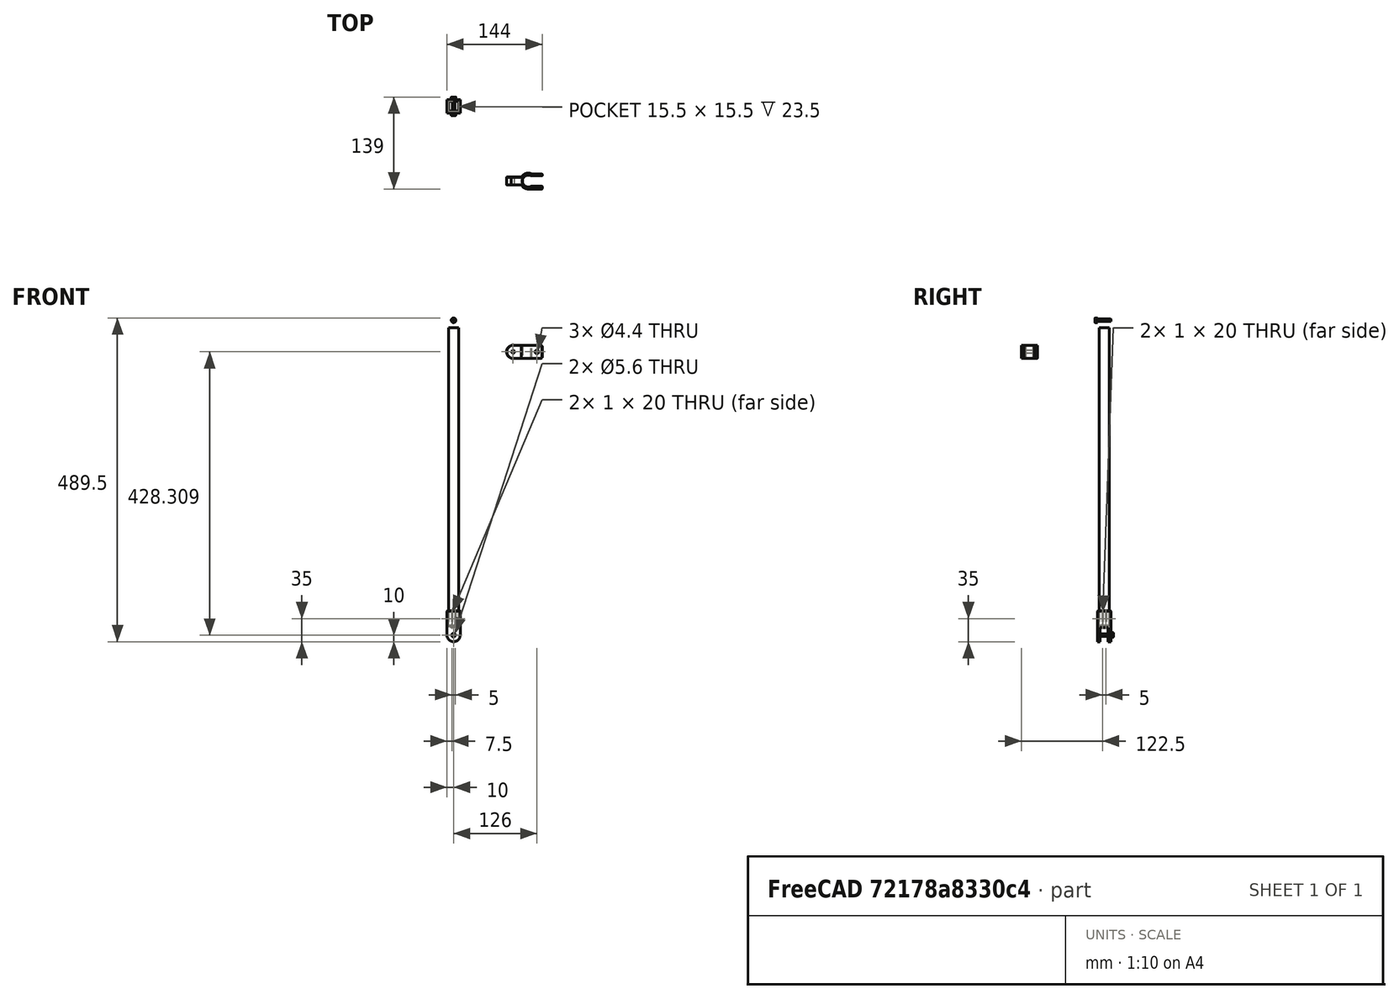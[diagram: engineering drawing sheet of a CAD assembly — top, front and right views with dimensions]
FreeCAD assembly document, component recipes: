
FREECAD ASSEMBLY — COMPONENT RECIPES ("BracePole")

This assembly document has 3 components, labeled P0..P2 below (a component is one placed body or linked part). 3 of them carry a construction recipe — the FreeCAD feature program that regenerates the part from scratch, quoted from this document or its linked companion documents; the rest are supplied as boundary geometry only. No exploded tour is included for this assembly.
COMPONENT P0 — recipe-attached ("SideArm_Pole", modeled in this document).
Construction recipe (the document's own serialized feature program — sketch geometry with constraints, then the solid features built on it; lengths are millimeters unless a unit is written):

FEATURE [PartDesign::AdditiveBox] Box003  label="SideArm_Pole_Base"
  AttacherType = Attacher::AttachEngine3D
  AttachmentOffset = pos=(-7.5,-7.5,0) rot=(0,0,1;0rad)
  Height = 450
  Length = 15
  MapMode = 5
  Placement = pos=(-7.5,-7.5,0) rot=(0,0,1;0rad)
  Support = -> [XY_Plane093]
  Width = 15
  expr: .AttachmentOffset.Base.x = -<<Common>>#<<Parameters>>.pri_bracepole / 2
  expr: .AttachmentOffset.Base.y = -<<Common>>#<<Parameters>>.pri_bracepole / 2
  expr: Height = <<Common>>#<<Parameters>>.pri_bracelength
  expr: Length = <<Common>>#<<Parameters>>.pri_bracepole
  expr: Width = <<Common>>#<<Parameters>>.pri_bracepole
FEATURE [PartDesign::CoordinateSystem] Local_CS310  label="LCSp_SideArm_Pole_Bottom"
  AttacherType = Attacher::AttachEngine3D
  MapMode = 2
  Support = -> [XY_Plane093]
FEATURE [PartDesign::CoordinateSystem] Local_CS311  label="LCSp_SideArm_Pole_Top"
  AttacherType = Attacher::AttachEngine3D
  AttachmentOffset = pos=(0,0,-450) rot=(0,0,1;0rad)
  MapMode = 5
  Placement = pos=(0,0,450) rot=(0,1,0;3.14159rad)
  Support = -> [XY_Plane093]
  expr: .AttachmentOffset.Base.z = -<<Common>>#<<Parameters>>.pri_bracelength
FEATURE [PartDesign::Body] Body022041  label="SideArm_Pole"
  Group = -> [Box003,Local_CS310,Local_CS311]
  Origin = -> Origin094
  Placement = pos=(0,0,15) rot=(0,0,1;0rad)
  Tip = -> Box003
COMPONENT P1 — recipe-attached ("SideArm_PoleClamp", modeled in this document).
Construction recipe (the document's own serialized feature program — sketch geometry with constraints, then the solid features built on it; lengths are millimeters unless a unit is written):

FEATURE [Sketcher::SketchObject] Sketch194  label="SideArm_PoleClamp_Base_Sketch"
  FullyConstrained = true
  MapMode = 5
  Support = -> [XY_Plane094]
  expr: .Constraints.innerdia = <<Common>>#<<Parameters>>.sec_poledia
  expr: Constraints[23] = <<Common>>#<<Parameters>>.sec_poledia - 2
  expr: Constraints[27] = <<Common>>#<<Parameters>>.sec_sidebolt * 2
  expr: Constraints[31] = <<Common>>#<<Parameters>>.sec_fthick
  expr: Constraints[32] = <<Common>>#<<Parameters>>.pri_bracepivotdia - (<<Common>>#<<Parameters>>.sec_fthick + 1) * 2
  expr: Constraints[36] = <<Common>>#<<Parameters>>.sec_poledia
  expr: Constraints[39] = <<Common>>#<<Parameters>>.sec_sidebolt
  expr: Constraints[42] = <<Common>>#<<Parameters>>.sec_fthick + 1
  expr: Constraints[43] = <<Common>>#<<Parameters>>.pri_bracepivotdia + <<Common>>#<<Parameters>>.sec_fthick + <<Common>>#<<Parameters>>.pri_poledia / 2
  sketch-geometry (17):
    g0: ArcOfCircle CenterX=0 CenterY=0 CenterZ=0 NormalX=0 NormalY=0 NormalZ=1 AngleXU=0 Radius=9 StartAngle=1.09491 EndAngle=5.18827
    g1: LineSegment StartX=4.12311 StartY=8 StartZ=0 EndX=21 EndY=8 EndZ=0
    g2: LineSegment StartX=4.12311 StartY=-8 StartZ=0 EndX=21 EndY=-8 EndZ=0
    g3: LineSegment StartX=21 StartY=8 StartZ=0 EndX=21 EndY=10.6667 EndZ=0
    g4: LineSegment StartX=21 StartY=10.6667 StartZ=0 EndX=5.49747 EndY=10.6667 EndZ=0
    g5: ArcOfCircle CenterX=0 CenterY=0 CenterZ=0 NormalX=0 NormalY=0 NormalZ=1 AngleXU=0 Radius=12 StartAngle=1.09491 EndAngle=2.61799
    g6: LineSegment StartX=-10.3923 StartY=6 StartZ=0 EndX=-33 EndY=6 EndZ=0
    g7: LineSegment StartX=-33 StartY=-6 StartZ=0 EndX=-10.3923 EndY=-6 EndZ=0
    g8: LineSegment StartX=21 StartY=-8 StartZ=0 EndX=21 EndY=-12 EndZ=0
    g9: ArcOfCircle CenterX=0 CenterY=0 CenterZ=0 NormalX=0 NormalY=0 NormalZ=1 AngleXU=0 Radius=12 StartAngle=3.66519 EndAngle=4.71239
    g10: LineSegment StartX=-3.33968e-05 StartY=-12 StartZ=0 EndX=21 EndY=-12 EndZ=0
    g11: GeomPoint X=13 Y=10.6667 Z=0
    g12: LineSegment StartX=0 StartY=0 StartZ=0 EndX=5.49747 EndY=10.6667 EndZ=0
    g13: GeomPoint X=-9 Y=0 Z=0
    g14: Circle CenterX=0 CenterY=0 CenterZ=0 NormalX=0 NormalY=0 NormalZ=1 AngleXU=0 Radius=9
    g15: GeomPoint X=9 Y=0 Z=0
    g16: LineSegment StartX=-33 StartY=6 StartZ=0 EndX=-33 EndY=-6 EndZ=0
  constraints (44):
    c: Coincident(g0,g-1)
    c: Diameter(g0) = 18  'innerdia'
    c: Coincident(g1,g0)
    c: Horizontal(g1)
    c: Coincident(g2,g0)
    c: Horizontal(g2)
    c: Coincident(g3,g1)
    c: Vertical(g3)
    c: Horizontal(g4)
    c: Coincident(g5,g0)
    c: Coincident(g5,g4)
    c: Coincident(g6,g5)
    c: Horizontal(g6)
    c: Horizontal(g7)
    c: Coincident(g8,g2)
    c: Vertical(g8)
    c: Coincident(g9,g0)
    c: Coincident(g9,g7)
    c: Coincident(g10,g9)
    c: Horizontal(g10)
    c: Equal(g9,g5)
    c: Symmetric(g6,g7,g-1)
    c: Symmetric(g1,g2,g-1)
    c: DistanceY(g2,g1) = 16
    c: Coincident(g3,g4)
    c: Coincident(g8,g10)
    c: PointOnObject(g11,g4)
    c: DistanceX(g11,g3) = 8
    c: Coincident(g12,g0)
    c: Coincident(g12,g4)
    c: PointOnObject(g0,g12)
    c: Distance(g0,g4) = 3
    c: DistanceY(g7,g6) = 12
    c: PointOnObject(g13,g0)
    c: PointOnObject(g13,g-1)
    c: Coincident(g14,g0)
    c: Diameter(g14) = 18
    c: PointOnObject(g15,g14)
    c: PointOnObject(g15,g-1)
    c: DistanceX(g15,g11) = 4
    c: Coincident(g16,g6)
    c: Coincident(g16,g7)
    c: DistanceY(g8,g8) = 4
    c: DistanceX(g6,g0) = 33
FEATURE [PartDesign::Pad] Pad048  label="SideArm_PoleClamp_Base"
  Direction = (0,0,1)
  Length = 20
  Length2 = 10
  Midplane = true
  Profile = -> Sketch194
  Type = 0
  expr: Length = <<Common>>#<<Parameters>>.pri_bracepivotdia
FEATURE [Sketcher::SketchObject] Sketch195  label="SideArm_PoleClamp_Pivot_Sketch"
  ExternalGeometry = -> [Pad048]
  FullyConstrained = true
  MapMode = 5
  Placement = pos=(0,0,0) rot=(1,0,0;1.5708rad)
  Support = -> [XZ_Plane095]
  expr: Constraints[11] = <<Common>>#<<Parameters>>.pri_bracepivotdia
  expr: Constraints[14] = <<Common>>#<<Parameters>>.sec_sidebolt * 1.1
  expr: Constraints[45] = <<Common>>#<<Parameters>>.pri_fillet
  expr: Constraints[67] = <<Common>>#<<Parameters>>.pri_fillet
  sketch-geometry (28):
    g0: ArcOfCircle CenterX=-23 CenterY=0 CenterZ=0 NormalX=0 NormalY=0 NormalZ=1 AngleXU=0 Radius=10 StartAngle=2.0944 EndAngle=4.18879
    g1: LineSegment StartX=-33 StartY=10 StartZ=0 EndX=21 EndY=10 EndZ=0
    g2: LineSegment StartX=-33 StartY=-10 StartZ=0 EndX=21 EndY=-10 EndZ=0
    g3: LineSegment StartX=-25.6795 StartY=-10 StartZ=0 EndX=-25.6795 EndY=-11 EndZ=0
    g4: LineSegment StartX=-25.6795 StartY=-11 StartZ=0 EndX=-34 EndY=-11 EndZ=0
    g5: LineSegment StartX=-34 StartY=-11 StartZ=0 EndX=-34 EndY=11 EndZ=0
    g6: LineSegment StartX=-34 StartY=11 StartZ=0 EndX=-25.6795 EndY=11 EndZ=0
    g7: LineSegment StartX=-25.6795 StartY=11 StartZ=0 EndX=-25.6795 EndY=10 EndZ=0
    g8: GeomPoint X=-33 Y=0 Z=0
    g9: Circle CenterX=13 CenterY=0 CenterZ=0 NormalX=0 NormalY=0 NormalZ=1 AngleXU=0 Radius=2.2
    g10: ArcOfCircle CenterX=18.5 CenterY=7.5 CenterZ=0 NormalX=0 NormalY=0 NormalZ=1 AngleXU=0 Radius=2.5 StartAngle=0 EndAngle=0.785398
    g11: ArcOfCircle CenterX=18.5 CenterY=-7.5 CenterZ=0 NormalX=0 NormalY=0 NormalZ=1 AngleXU=0 Radius=2.5 StartAngle=5.49779 EndAngle=6.28319
    g12: LineSegment StartX=18.5 StartY=10 StartZ=0 EndX=18.5 EndY=-10 EndZ=0
    g13: LineSegment StartX=18.5 StartY=-7.5 StartZ=0 EndX=21 EndY=-7.5 EndZ=0
    g14: LineSegment StartX=18.5 StartY=7.5 StartZ=0 EndX=21 EndY=7.5 EndZ=0
    g15: LineSegment StartX=19.5355 StartY=10 StartZ=0 EndX=19.5355 EndY=11 EndZ=0
    g16: LineSegment StartX=19.5355 StartY=11 StartZ=0 EndX=22 EndY=11 EndZ=0
    g17: LineSegment StartX=22 StartY=11 StartZ=0 EndX=22 EndY=-11 EndZ=0
    g18: LineSegment StartX=22 StartY=-11 StartZ=0 EndX=19.5355 EndY=-11 EndZ=0
    g19: LineSegment StartX=19.5355 StartY=-11 StartZ=0 EndX=19.5355 EndY=-10 EndZ=0
    g20: LineSegment StartX=21 StartY=-7.5 StartZ=0 EndX=21 EndY=7.5 EndZ=0
    g21: LineSegment StartX=-33 StartY=0 StartZ=0 EndX=-23 EndY=0 EndZ=0
    g22: Circle CenterX=-23 CenterY=0 CenterZ=0 NormalX=0 NormalY=0 NormalZ=1 AngleXU=0 Radius=2.2
    g23: LineSegment StartX=-28 StartY=-8.66025 StartZ=0 EndX=-25.6795 EndY=-10 EndZ=0
    g24: LineSegment StartX=-28 StartY=8.66025 StartZ=0 EndX=-25.6795 EndY=10 EndZ=0
    g25: LineSegment StartX=-25.6795 StartY=10 StartZ=0 EndX=-25.6795 EndY=-10 EndZ=0
    g26: LineSegment StartX=19.5355 StartY=10 StartZ=0 EndX=20.2678 EndY=9.26777 EndZ=0
    g27: LineSegment StartX=19.5355 StartY=-10 StartZ=0 EndX=20.2678 EndY=-9.26777 EndZ=0
  constraints (77):
    c: PointOnObject(g3,g2)
    c: Coincident(g4,g3)
    c: Horizontal(g4)
    c: Coincident(g5,g4)
    c: Vertical(g5)
    c: Coincident(g6,g5)
    c: Horizontal(g6)
    c: Coincident(g7,g6)
    c: Vertical(g7)
    c: Vertical(g3)
    c: Equal(g3,g7)
    c: Diameter(g0) = 20
    c: DistanceY(g7,g7) = 1
    c: DistanceX(g5,g1) = 1
    c: Diameter(g9) = 4.4
    c: Vertical(g12)
    c: Coincident(g13,g11)
    c: Coincident(g13,g11)
    c: Coincident(g14,g10)
    c: Coincident(g14,g10)
    c: Horizontal(g14)
    c: PointOnObject(g10,g12)
    c: PointOnObject(g11,g12)
    c: Horizontal(g13)
    c: Vertical(g15)
    c: Coincident(g16,g15)
    c: Horizontal(g16)
    c: Coincident(g17,g16)
    c: Vertical(g17)
    c: Coincident(g18,g17)
    c: Horizontal(g18)
    c: Vertical(g19)
    c: Coincident(g20,g11)
    c: Coincident(g20,g10)
    c: Equal(g15,g19)
    c: PointOnObject(g6,g16)
    c: DistanceX(g1,g16) = 1
    c: Coincident(g18,g19)
    c: PointOnObject(g8,g0)
    c: Coincident(g21,g8)
    c: Coincident(g21,g0)
    c: Horizontal(g21)
    c: PointOnObject(g3,g7)
    c: PointOnObject(g9,g-1)
    c: DistanceX(g9,g1) = 8
    c: Radius(g10) = 2.5
    c: Coincident(g1,g-3)
    c: Coincident(g2,g-3)
    c: Coincident(g2,g-4)
    c: Coincident(g1,g-4)
    c: PointOnObject(g11,g-3)
    c: PointOnObject(g10,g-3)
    c: PointOnObject(g8,g-4)
    c: Coincident(g22,g0)
    c: Equal(g22,g9)
    c: DistanceX(g0,g-1) = 23  'Clamp_Pivot_Distance'
    c: PointOnObject(g0,g-1)
    c: Tangent(g24,g0) = 1.5708
    c: Tangent(g23,g0) = -1.5708
    c: Tangent(g27,g11) = -1.5708
    c: Tangent(g26,g10) = 1.5708
    c: PointOnObject(g12,g2)
    c: Coincident(g19,g27)
    c: PointOnObject(g12,g1)
    c: Coincident(g15,g26)
    c: Angle(g1,g26) = 2.35619
    c: PointOnObject(g15,g1)
    c: DistanceY(g10,g12) = 2.5
    c: PointOnObject(g19,g2)
    c: Equal(g27,g26)
    c: PointOnObject(g18,g15)
    c: Coincident(g7,g24)
    c: Coincident(g7,g25)
    c: PointOnObject(g7,g1)
    c: Coincident(g3,g23)
    c: Angle(g2,g23) = 2.61799
    c: Coincident(g25,g3)
FEATURE [PartDesign::Pocket] Pocket126  label="SideArm_PoleClamp_Pivot"
  BaseFeature = -> Pad048
  Direction = (0,1,2e-16)
  Length = 5
  Length2 = 5
  Midplane = true
  Profile = -> Sketch195
  Type = 1
FEATURE [PartDesign::CoordinateSystem] Local_CS268  label="LCS_SideClamp_Pivot"
  AttacherType = Attacher::AttachEngine3D
  MapMode = 45
  Placement = pos=(-23,0,1e-16) rot=(0.707107,0,0.707107;3.14159rad)
  Support = -> [Pocket126]
FEATURE [PartDesign::CoordinateSystem] Local_CS269  label="LCS_SideClamp_Bolt"
  AttacherType = Attacher::AttachEngine3D
  MapMode = 11
  Placement = pos=(13,10.6667,2.4e-15) rot=(-0.57735,0.57735,0.57735;2.0944rad)
  Support = -> [Pocket126]
FEATURE [PartDesign::Plane] DatumPlane059  label="DatumPlane_SideClamp_Nut"
  Length = 60.7703
  MapMode = 11
  Placement = pos=(13,-12,-2.7e-15) rot=(0.57735,-0.57735,0.57735;2.0944rad)
  ResizeMode = 0
  Support = -> [Pocket126]
  Width = 68.7703
FEATURE [Sketcher::SketchObject] Sketch238  label="SideArm_PoleClamp_BraceNut_Sketch"
  FullyConstrained = true
  MapMode = 5
  Placement = pos=(13,-12,-2.7e-15) rot=(-0.57735,0.57735,-0.57735;4.18879rad)
  Support = -> [DatumPlane059]
  expr: Constraints[1] = <<Common>>#<<Parameters>>.acc_M4Bore
  sketch-geometry (1):
    g0: Circle CenterX=0 CenterY=0 CenterZ=0 NormalX=0 NormalY=0 NormalZ=1 AngleXU=0 Radius=2.8
  constraints (2):
    c: Coincident(g0,g-1)
    c: Diameter(g0) = 5.6
FEATURE [PartDesign::Pocket] Pocket188  label="SideArm_PoleClamp_BraceNut"
  BaseFeature = -> Pocket126
  Direction = (0,1,0)
  Length = 4
  Length2 = 100
  Profile = -> Sketch238
  Type = 0
FEATURE [PartDesign::CoordinateSystem] Local_CS320  label="LCS_SideClamp_Nut"
  AttacherType = Attacher::AttachEngine3D
  MapMode = 11
  Placement = pos=(13,-12,-2.7e-15) rot=(-0.57735,0.57735,0.57735;2.0944rad)
  Support = -> [Pocket126]
FEATURE [PartDesign::Chamfer] Chamfer001  label="SideArm_Chamfer"
  Angle = 45
  Base = -> Pocket188 [Edge6,Edge37,Edge36,Edge35,Edge32,Edge33,Edge31,Edge29,Edge28,Edge10,Edge12,Edge9,Edge13,Edge14,Edge16,Edge17,Edge18,Edge1,Edge5,Edge4,Edge3,Edge2,Edge26,Edge24,Edge22,Edge20,Edge66,Edge68,Edge67,Edge65,Edge62,Edge58,Edge60,Edge59,Edge57,Edge56,Edge47,Edge42,Edge41,Edge49,+6 more]
  BaseFeature = -> Pocket188
  ChamferType = 0
  FlipDirection = false
  Size = 0.4
  Size2 = 1
  SupportTransform = false
  UseAllEdges = false
FEATURE [PartDesign::Body] Body022042  label="SideArm_PoleClamp"
  Group = -> [Sketch194,Pad048,Sketch195,Pocket126,Local_CS268,Local_CS269,Sketch238,DatumPlane059,Pocket188,Local_CS320,Chamfer001]
  Origin = -> Origin095
  Placement = pos=(113,-113,428.309) rot=(0,0,1;0rad)
  Tip = -> Chamfer001
  expr: .Placement.Base.x = <<Common>>#<<Parameters>>.bolt_x
  expr: .Placement.Base.y = -<<Common>>#<<Parameters>>.bolt_y
  expr: .Placement.Base.z = <<Common>>#<<Parameters>>.pri_braceclamp_z
COMPONENT P2 — recipe-attached ("SideArm_Pivot_Outer_Square", modeled in this document).
Construction recipe (the document's own serialized feature program — sketch geometry with constraints, then the solid features built on it; lengths are millimeters unless a unit is written):

FEATURE [Sketcher::SketchObject] Sketch263  label="SideArm_Outer_YZ_Sketch"
  FullyConstrained = true
  MapMode = 5
  Placement = pos=(0,0,0) rot=(0.57735,0.57735,0.57735;2.0944rad)
  Support = -> [YZ_Plane113]
  expr: Constraints[12] = -<<Common>>#<<Parameters>>.pri_bracepivotdia / 2 - 1
  expr: Constraints[19] = <<Common>>#<<Parameters>>.pri_bracepivotdia / 2 + <<Common>>#<<Parameters>>.sec_fthick / 2
  expr: Constraints[22] = max(<<Common>>#<<Parameters>>.pri_bracepole + <<Common>>#<<Parameters>>.sec_fthick; <<Common>>#<<Parameters>>.pri_bracepivotdia + 1) + 2
  expr: Constraints[23] = <<Common>>#<<Parameters>>.pri_bracepivotdia
  expr: Constraints[35] = <<Common>>#<<Parameters>>.sec_fthick + 1
  sketch-geometry (14):
    g0: LineSegment StartX=-6 StartY=11.5 StartZ=0 EndX=-6 EndY=-11 EndZ=0
    g1: LineSegment StartX=-6 StartY=-11 StartZ=0 EndX=6 EndY=-11 EndZ=0
    g2: LineSegment StartX=6 StartY=-11 StartZ=0 EndX=6 EndY=11.5 EndZ=0
    g3: LineSegment StartX=10 StartY=11.5 StartZ=0 EndX=11.5 EndY=13 EndZ=0
    g4: LineSegment StartX=11.5 StartY=13 StartZ=0 EndX=11.5 EndY=-13 EndZ=0
    g5: LineSegment StartX=11.5 StartY=-13 StartZ=0 EndX=-11.5 EndY=-13 EndZ=0
    g6: LineSegment StartX=-11.5 StartY=-13 StartZ=0 EndX=-11.5 EndY=13 EndZ=0
    g7: LineSegment StartX=-11.5 StartY=13 StartZ=0 EndX=-10 EndY=11.5 EndZ=0
    g8: LineSegment StartX=-6 StartY=11.5 StartZ=0 EndX=6 EndY=11.5 EndZ=0
    g9: LineSegment StartX=-11.5 StartY=13 StartZ=0 EndX=11.5 EndY=13 EndZ=0
    g10: LineSegment StartX=-10 StartY=11.5 StartZ=0 EndX=-10 EndY=-11 EndZ=0
    g11: LineSegment StartX=10 StartY=11.5 StartZ=0 EndX=10 EndY=-11 EndZ=0
    g12: LineSegment StartX=10 StartY=-11 StartZ=0 EndX=6 EndY=-11 EndZ=0
    g13: LineSegment StartX=-10 StartY=-11 StartZ=0 EndX=-6 EndY=-11 EndZ=0
  constraints (39):
    c: Vertical(g0)
    c: Coincident(g1,g0)
    c: Horizontal(g1)
    c: Coincident(g2,g1)
    c: Vertical(g2)
    c: Coincident(g4,g3)
    c: Vertical(g4)
    c: Coincident(g5,g4)
    c: Horizontal(g5)
    c: Coincident(g6,g5)
    c: Vertical(g6)
    c: Coincident(g7,g6)
    c: DistanceY(g1) = -11
    c: Coincident(g8,g0)
    c: Coincident(g8,g2)
    c: Coincident(g9,g6)
    c: Coincident(g9,g3)
    c: Horizontal(g8)
    c: Equal(g7,g3)
    c: DistanceY(g2) = 11.5
    c: Symmetric(g3,g6,g-2)
    c: DistanceY(g4,g1) = 2
    c: DistanceX(g5,g5) = 23
    c: DistanceX(g7,g3) = 20
    c: Vertical(g10)
    c: Coincident(g11,g3)
    c: Vertical(g11)
    c: Coincident(g12,g11)
    c: Coincident(g12,g2)
    c: Horizontal(g12)
    c: Coincident(g13,g10)
    c: Coincident(g13,g0)
    c: Horizontal(g13)
    c: Coincident(g10,g7)
    c: Equal(g12,g13)
    c: DistanceX(g12,g12) = 4
    c: PointOnObject(g7,g8)
    c: PointOnObject(g3,g8)
    c: Angle(g3,g4) = 0.785398
FEATURE [Sketcher::SketchObject] Sketch264  label="SideArm_Outer_Profile_XZ_Sketch"
  FullyConstrained = true
  MapMode = 5
  Placement = pos=(0,0,0) rot=(1,0,0;1.5708rad)
  Support = -> [XZ_Plane113]
  expr: Constraints[10] = <<Common>>#<<Parameters>>.pri_bracepivotdia
  expr: Constraints[13] = <<Common>>#<<Parameters>>.pri_bracepivotdia / 2 + <<Common>>#<<Parameters>>.sec_fthick / 2
  expr: Constraints[15] = <<Common>>#<<Parameters>>.pri_bracepivotdia
  expr: Constraints[18] = min(<<Common>>#<<Parameters>>.pri_bracepole + <<Common>>#<<Parameters>>.sec_fthick * 2; 20)
  expr: Constraints[22] = max(0.5; abs(20 - <<Common>>#<<Parameters>>.pri_bracepivotdia) / 2)
  expr: Constraints[27] = <<Common>>#<<Parameters>>.sec_sidebolt * 1.1
  sketch-geometry (11):
    g0: ArcOfCircle CenterX=0 CenterY=0 CenterZ=0 NormalX=0 NormalY=0 NormalZ=1 AngleXU=0 Radius=10 StartAngle=3.1416 EndAngle=6.28319
    g1: LineSegment StartX=10 StartY=-2.4e-15 StartZ=0 EndX=10 EndY=11.5 EndZ=0
    g2: LineSegment StartX=-10 StartY=-4.17172e-05 StartZ=0 EndX=-10 EndY=11.5 EndZ=0
    g3: LineSegment StartX=-10 StartY=11.5 StartZ=0 EndX=-10 EndY=12 EndZ=0
    g4: LineSegment StartX=-10 StartY=12 StartZ=0 EndX=-10 EndY=36.5 EndZ=0
    g5: LineSegment StartX=-10 StartY=36.5 StartZ=0 EndX=10 EndY=36.5 EndZ=0
    g6: LineSegment StartX=10 StartY=36.5 StartZ=0 EndX=10 EndY=12 EndZ=0
    g7: LineSegment StartX=10 StartY=12 StartZ=0 EndX=10 EndY=11.5 EndZ=0
    g8: LineSegment StartX=0 StartY=0 StartZ=0 EndX=10 EndY=-2.4e-15 EndZ=0
    g9: LineSegment StartX=-10 StartY=12 StartZ=0 EndX=10 EndY=12 EndZ=0
    g10: Circle CenterX=0 CenterY=0 CenterZ=0 NormalX=0 NormalY=0 NormalZ=1 AngleXU=0 Radius=2.2
  constraints (28):
    c: Coincident(g0,g-1)
    c: Coincident(g1,g0)
    c: Coincident(g3,g2)
    c: Coincident(g4,g3)
    c: Vertical(g4)
    c: Coincident(g5,g4)
    c: Coincident(g6,g5)
    c: Coincident(g7,g6)
    c: Coincident(g7,g1)
    c: Vertical(g6)
    c: Diameter(g0) = 20
    c: Coincident(g8,g0)
    c: Coincident(g8,g0)
    c: DistanceY(g-1,g1) = 11.5
    c: Symmetric(g2,g1,g-2)
    c: DistanceX(g2,g1) = 20
    c: Perpendicular(g1,g8)
    c: Symmetric(g4,g5,g-2)
    c: DistanceX(g5,g5) = 20
    c: Coincident(g9,g3)
    c: Coincident(g9,g6)
    c: Horizontal(g9)
    c: DistanceY(g2,g3) = 0.5
    c: DistanceY(g1,g5) = 25
    c: Coincident(g0,g2)
    c: Vertical(g2)
    c: Coincident(g10,g0)
    c: Diameter(g10) = 4.4
FEATURE [Sketcher::SketchObject] Sketch265  label="SideArm_Outer_Shaft_Sketch"
  AttachmentOffset = pos=(0,0,13) rot=(0,0,1;0rad)
  FullyConstrained = true
  MapMode = 5
  Placement = pos=(0,0,13) rot=(0,0,1;0rad)
  Support = -> [XY_Plane113]
  expr: .AttachmentOffset.Base.z = <<Common>>#<<Parameters>>.pri_bracepivotdia / 2 + <<Common>>#<<Parameters>>.sec_fthick * 1 + (20 - <<Common>>#<<Parameters>>.pri_bracepivotdia) / 2
  expr: Constraints[9] = <<Common>>#<<Parameters>>.pri_bracepole + <<Common>>#<<Parameters>>.pri_tol
  sketch-geometry (4):
    g0: LineSegment StartX=-7.75 StartY=7.75 StartZ=0 EndX=7.75 EndY=7.75 EndZ=0
    g1: LineSegment StartX=7.75 StartY=7.75 StartZ=0 EndX=7.75 EndY=-7.75 EndZ=0
    g2: LineSegment StartX=7.75 StartY=-7.75 StartZ=0 EndX=-7.75 EndY=-7.75 EndZ=0
    g3: LineSegment StartX=-7.75 StartY=-7.75 StartZ=0 EndX=-7.75 EndY=7.75 EndZ=0
  constraints (10):
    c: Coincident(g0,g1)
    c: Coincident(g1,g2)
    c: Coincident(g2,g3)
    c: Coincident(g3,g0)
    c: Horizontal(g2)
    c: Vertical(g3)
    c: Equal(g0,g1)
    c: Symmetric(g0,g0,g-2)
    c: Symmetric(g0,g1,g-1)
    c: DistanceX(g0,g0) = 15.5
FEATURE [PartDesign::CoordinateSystem] Local_CS315  label="LCSp_Sidearm_Pivot_Lower001"
  AttacherType = Attacher::AttachEngine3D
  MapMode = 5
  Placement = pos=(0,0,0) rot=(0,1,0;3.14159rad)
  Support = -> [XY_Plane113]
FEATURE [PartDesign::CoordinateSystem] Local_CS316  label="LCSp_Sidearm_Pivot_LowerTilt001"
  AttacherType = Attacher::AttachEngine3D
  AttachmentOffset = pos=(0,0,0) rot=(0,-1,0;0.440587rad)
  MapMode = 5
  Placement = pos=(0,0,0) rot=(0,1,0;2.70101rad)
  Support = -> [Local_CS315]
  expr: .AttachmentOffset.Rotation.Pitch = -<<Common>>#<<Parameters>>.pri_bracetilt
FEATURE [PartDesign::Pad] Pad066  label="SideArm_Outer_Body"
  Direction = (0,-1,-2e-16)
  Length = 20
  Length2 = 100
  Midplane = true
  Placement = pos=(0,0,0) rot=(1,0,0;1.5708rad)
  Profile = -> Sketch264
  Type = 0
  expr: Length = min(<<Common>>#<<Parameters>>.pri_bracepole + <<Common>>#<<Parameters>>.sec_fthick * 2; 20)
FEATURE [PartDesign::Pocket] Pocket176  label="SideArm_Outer_YZ_Cut"
  BaseFeature = -> Pad066
  Direction = (-1,2e-16,-3e-16)
  Length = 5
  Length2 = 100
  Midplane = true
  Placement = pos=(0,0,0) rot=(1,0,0;1.5708rad)
  Profile = -> Sketch263
  Type = 1
FEATURE [PartDesign::Pocket] Pocket177  label="SideArm_Outer_Shaft"
  BaseFeature = -> Pocket176
  Direction = (0,0,-1)
  Length = 5
  Length2 = 100
  Placement = pos=(0,0,0) rot=(1,0,0;1.5708rad)
  Profile = -> Sketch265
  Reversed = true
  Type = 1
FEATURE [PartDesign::AdditiveCylinder] Cylinder014  label="SideArm_Outer_GripCylinderX1"
  Angle = 360
  AttacherType = Attacher::AttachEngine3D
  AttachmentOffset = pos=(7.75,-2.5,15) rot=(0,0,1;0rad)
  BaseFeature = -> Pocket177
  FirstAngle = 0
  Height = 20
  MapMode = 5
  Placement = pos=(7.75,-2.5,15) rot=(0,0,1;0rad)
  Radius = 0.5
  SecondAngle = 0
  Support = -> [XY_Plane113]
  expr: .AttachmentOffset.Base.x = (<<Common>>#<<Parameters>>.pri_bracepole + <<Common>>#<<Parameters>>.pri_tol) / 2
  expr: .AttachmentOffset.Base.z = <<Common>>#<<Parameters>>.pri_bracepivotdia / 2 + <<Common>>#<<Parameters>>.sec_fthick * 1 + (20 - <<Common>>#<<Parameters>>.pri_bracepivotdia) / 2 + 2
FEATURE [PartDesign::AdditiveCylinder] Cylinder015  label="SideArrn_Outer_GripCylinderX2"
  Angle = 360
  AttacherType = Attacher::AttachEngine3D
  AttachmentOffset = pos=(7.75,2.5,15) rot=(0,0,1;0rad)
  BaseFeature = -> Cylinder014
  FirstAngle = 0
  Height = 20
  MapMode = 5
  Placement = pos=(7.75,2.5,15) rot=(0,0,1;0rad)
  Radius = 0.5
  SecondAngle = 0
  Support = -> [XY_Plane113]
  expr: .AttachmentOffset.Base.x = (<<Common>>#<<Parameters>>.pri_bracepole + <<Common>>#<<Parameters>>.pri_tol) / 2
  expr: .AttachmentOffset.Base.z = <<Common>>#<<Parameters>>.pri_bracepivotdia / 2 + <<Common>>#<<Parameters>>.sec_fthick * 1 + (20 - <<Common>>#<<Parameters>>.pri_bracepivotdia) / 2 + 2
FEATURE [PartDesign::PolarPattern] PolarPattern005  label="SideArm_Outer_GripCylinder"
  Angle = 360
  Axis = -> Z_Axis113
  BaseFeature = -> Cylinder015
  Occurrences = 4
  Originals = -> [Cylinder014,Cylinder015]
  Placement = pos=(7.75,2.5,15) rot=(0,0,1;0rad)
FEATURE [PartDesign::CoordinateSystem] Local_CS317  label="LCSp_SideArm_Pivot_OuterTilt"
  AttacherType = Attacher::AttachEngine3D
  AttachmentOffset = pos=(0,0,0) rot=(0,1,0;0.440587rad)
  MapMode = 5
  Placement = pos=(0,0,0) rot=(0,1,0;3.58218rad)
  Support = -> [Local_CS315]
  expr: .AttachmentOffset.Rotation.Pitch = <<Common>>#<<Parameters>>.pri_bracetilt
FEATURE [Sketcher::SketchObject] Sketch268  label="SideArm_Outer_SupportA_Sketch"
  AttachmentOffset = pos=(0,0,14.5) rot=(0,0,1;0rad)
  FullyConstrained = true
  MapMode = 5
  Placement = pos=(0,0,14.5) rot=(0,0,1;0rad)
  Support = -> [XY_Plane113]
  expr: .AttachmentOffset.Base.z = <<Common>>#<<Parameters>>.pri_bracepivotdia / 2 + <<Common>>#<<Parameters>>.sec_fthick * 1.5 + (20 - <<Common>>#<<Parameters>>.pri_bracepivotdia) / 2
  sketch-geometry (4):
    g0: LineSegment StartX=-2.25 StartY=2.25 StartZ=0 EndX=2.25 EndY=2.25 EndZ=0
    g1: LineSegment StartX=2.25 StartY=2.25 StartZ=0 EndX=2.25 EndY=-2.25 EndZ=0
    g2: LineSegment StartX=2.25 StartY=-2.25 StartZ=0 EndX=-2.25 EndY=-2.25 EndZ=0
    g3: LineSegment StartX=-2.25 StartY=-2.25 StartZ=0 EndX=-2.25 EndY=2.25 EndZ=0
  constraints (10):
    c: Coincident(g0,g1)
    c: Coincident(g1,g2)
    c: Coincident(g2,g3)
    c: Coincident(g3,g0)
    c: Horizontal(g0)
    c: Vertical(g3)
    c: Symmetric(g1,g0,g-1)
    c: Symmetric(g1,g2,g-2)
    c: Equal(g0,g3)
    c: DistanceY(g1,g1) = 4.5
FEATURE [Sketcher::SketchObject] Sketch269  label="SideArm_Outer_SupportB_Sketch"
  AttachmentOffset = pos=(0,0,14.75) rot=(0,0,1;0rad)
  FullyConstrained = true
  MapMode = 5
  Placement = pos=(0,0,14.75) rot=(0,0,1;0rad)
  Support = -> [XY_Plane113]
  expr: .AttachmentOffset.Base.z = <<Common>>#<<Parameters>>.pri_bracepivotdia / 2 + <<Common>>#<<Parameters>>.sec_fthick * 1.5 + (20 - <<Common>>#<<Parameters>>.pri_bracepivotdia) / 2 + 0.25
  expr: Constraints[8] = <<Common>>#<<Parameters>>.pri_bracepole + <<Common>>#<<Parameters>>.pri_tol
  sketch-geometry (13):
    g0: LineSegment StartX=-7.75 StartY=7.75 StartZ=0 EndX=7.75 EndY=7.75 EndZ=0
    g1: LineSegment StartX=7.75 StartY=7.75 StartZ=0 EndX=7.75 EndY=-7.75 EndZ=0
    g2: LineSegment StartX=7.75 StartY=-7.75 StartZ=0 EndX=-7.75 EndY=-7.75 EndZ=0
    g3: LineSegment StartX=-7.75 StartY=-7.75 StartZ=0 EndX=-7.75 EndY=7.75 EndZ=0
    g4: LineSegment StartX=-6.75 StartY=2.25 StartZ=0 EndX=2.25 EndY=2.25 EndZ=0
    g5: LineSegment StartX=-2.25 StartY=-2.25 StartZ=0 EndX=6.75 EndY=-2.25 EndZ=0
    g6: LineSegment StartX=-3.25 StartY=7.75 StartZ=0 EndX=7.75 EndY=-3.25 EndZ=0
    g7: LineSegment StartX=-7.75 StartY=3.25 StartZ=0 EndX=3.25 EndY=-7.75 EndZ=0
    g8: GeomPoint X=0 Y=2.25 Z=0
    g9: GeomPoint X=0 Y=-2.25 Z=0
    g10: LineSegment StartX=-2.25 StartY=-2.25 StartZ=0 EndX=2.25 EndY=2.25 EndZ=0
    g11: LineSegment StartX=-6.75 StartY=2.25 StartZ=0 EndX=-2.25 EndY=-2.25 EndZ=0
    g12: LineSegment StartX=2.25 StartY=2.25 StartZ=0 EndX=6.75 EndY=-2.25 EndZ=0
  constraints (35):
    c: Coincident(g0,g1)
    c: Coincident(g1,g2)
    c: Coincident(g2,g3)
    c: Coincident(g3,g0)
    c: Horizontal(g0)
    c: Vertical(g3)
    c: Symmetric(g0,g1,g-1)
    c: Symmetric(g1,g2,g-2)
    c: DistanceX(g2,g2) = 15.5
    c: Equal(g1,g2)
    c: Horizontal(g4)
    c: Horizontal(g5)
    c: PointOnObject(g6,g0)
    c: PointOnObject(g6,g1)
    c: PointOnObject(g7,g3)
    c: PointOnObject(g7,g2)
    c: PointOnObject(g8,g4)
    c: PointOnObject(g9,g5)
    c: PointOnObject(g9,g-2)
    c: Symmetric(g8,g9,g-1)
    c: DistanceY(g9,g8) = 4.5
    c: Coincident(g10,g5)
    c: Coincident(g10,g4)
    c: PointOnObject(g-1,g10)
    c: Angle(g10) = 0.785398
    c: PointOnObject(g5,g7)
    c: Perpendicular(g10,g7)
    c: PointOnObject(g4,g6)
    c: Perpendicular(g10,g6)
    c: PointOnObject(g4,g7)
    c: PointOnObject(g5,g6)
    c: Coincident(g11,g4)
    c: Coincident(g11,g5)
    c: Coincident(g12,g4)
    c: Coincident(g12,g5)
FEATURE [Sketcher::SketchObject] Sketch270  label="SideArm_Outer_SupportC_Sketch"
  AttachmentOffset = pos=(0,0,15) rot=(0,0,1;0rad)
  FullyConstrained = true
  MapMode = 5
  Placement = pos=(0,0,15) rot=(0,0,1;0rad)
  Support = -> [XY_Plane113]
  expr: .AttachmentOffset.Base.z = <<Common>>#<<Parameters>>.pri_bracepivotdia / 2 + <<Common>>#<<Parameters>>.sec_fthick * 1.5 + (20 - <<Common>>#<<Parameters>>.pri_bracepivotdia) / 2 + 0.5
  expr: Constraints[19] = <<Common>>#<<Parameters>>.pri_bracepole + <<Common>>#<<Parameters>>.pri_tol
  sketch-geometry (13):
    g0: LineSegment StartX=-2.25 StartY=2.25 StartZ=0 EndX=2.25 EndY=2.25 EndZ=0
    g1: LineSegment StartX=2.25 StartY=2.25 StartZ=0 EndX=2.25 EndY=-2.25 EndZ=0
    g2: LineSegment StartX=2.25 StartY=-2.25 StartZ=0 EndX=-2.25 EndY=-2.25 EndZ=0
    g3: LineSegment StartX=-2.25 StartY=-2.25 StartZ=0 EndX=-2.25 EndY=2.25 EndZ=0
    g4: LineSegment StartX=-7.75 StartY=7.75 StartZ=0 EndX=7.75 EndY=7.75 EndZ=0
    g5: LineSegment StartX=7.75 StartY=7.75 StartZ=0 EndX=7.75 EndY=-7.75 EndZ=0
    g6: LineSegment StartX=7.75 StartY=-7.75 StartZ=0 EndX=-7.75 EndY=-7.75 EndZ=0
    g7: LineSegment StartX=-7.75 StartY=-7.75 StartZ=0 EndX=-7.75 EndY=7.75 EndZ=0
    g8: LineSegment StartX=-3.25 StartY=7.75 StartZ=0 EndX=7.75 EndY=-3.25 EndZ=0
    g9: LineSegment StartX=-7.75 StartY=3.25 StartZ=0 EndX=3.25 EndY=-7.75 EndZ=0
    g10: LineSegment StartX=-2.25 StartY=-2.25 StartZ=0 EndX=2.25 EndY=2.25 EndZ=0
    g11: LineSegment StartX=-7.75 StartY=3.25 StartZ=0 EndX=-3.25 EndY=7.75 EndZ=0
    g12: LineSegment StartX=3.25 StartY=-7.75 StartZ=0 EndX=7.75 EndY=-3.25 EndZ=0
  constraints (34):
    c: Coincident(g0,g1)
    c: Coincident(g1,g2)
    c: Coincident(g2,g3)
    c: Coincident(g3,g0)
    c: Horizontal(g0)
    c: Vertical(g3)
    c: Symmetric(g2,g1,g-2)
    c: Symmetric(g1,g0,g-1)
    c: Equal(g1,g2)
    c: DistanceY(g1,g1) = 4.5
    c: Coincident(g4,g5)
    c: Coincident(g5,g6)
    c: Coincident(g6,g7)
    c: Coincident(g7,g4)
    c: Horizontal(g4)
    c: Vertical(g7)
    c: Symmetric(g5,g6,g-2)
    c: Symmetric(g4,g5,g-1)
    c: Equal(g5,g6)
    c: DistanceY(g5,g5) = 15.5
    c: PointOnObject(g8,g4)
    c: PointOnObject(g8,g5)
    c: PointOnObject(g9,g7)
    c: PointOnObject(g9,g6)
    c: PointOnObject(g2,g9)
    c: PointOnObject(g0,g8)
    c: Coincident(g10,g2)
    c: Coincident(g10,g0)
    c: Perpendicular(g8,g10)
    c: Perpendicular(g9,g10)
    c: Coincident(g11,g9)
    c: Coincident(g11,g8)
    c: Coincident(g12,g9)
    c: Coincident(g12,g8)
FEATURE [Sketcher::SketchObject] Sketch271  label="SideArm_Outer_Nut_Sketch"
  AttachmentOffset = pos=(0,0,10) rot=(0,0,1;0rad)
  FullyConstrained = true
  MapMode = 5
  Placement = pos=(0,-10,-2.2e-15) rot=(1,0,0;1.5708rad)
  Support = -> [XZ_Plane113]
  expr: Constraints[1] = <<Common>>#<<Parameters>>.acc_M4Bore
  sketch-geometry (1):
    g0: Circle CenterX=0 CenterY=0 CenterZ=0 NormalX=0 NormalY=0 NormalZ=1 AngleXU=0 Radius=2.8
  constraints (2):
    c: Coincident(g0,g-1)
    c: Diameter(g0) = 5.6
FEATURE [Sketcher::SketchObject] Sketch272  label="SideArm_Outer_Counterbore_Sketch"
  AttachmentOffset = pos=(0,0,-10) rot=(0,0,1;0rad)
  FullyConstrained = true
  MapMode = 5
  Placement = pos=(0,10,2.2e-15) rot=(1,0,0;1.5708rad)
  Support = -> [XZ_Plane113]
  sketch-geometry (1):
    g0: Circle CenterX=0 CenterY=0 CenterZ=0 NormalX=0 NormalY=0 NormalZ=1 AngleXU=0 Radius=4.5
  constraints (2):
    c: Coincident(g0,g-1)
    c: Radius(g0) = 4.5
FEATURE [PartDesign::Pocket] Pocket189  label="SideArm_Outer_Nut"
  BaseFeature = -> PolarPattern005
  Direction = (0,1,2e-16)
  Length = 4
  Length2 = 100
  Placement = pos=(7.75,2.5,15) rot=(0,0,1;0rad)
  Profile = -> Sketch271
  Type = 0
FEATURE [PartDesign::CoordinateSystem] Local_CS  label="LCS_SideArm_Outer_Nut"
  AttacherType = Attacher::AttachEngine3D
  MapMode = 11
  Placement = pos=(0,-10,-2e-15) rot=(0.57735,-0.57735,-0.57735;4.18879rad)
  Support = -> [Pocket189]
FEATURE [PartDesign::CoordinateSystem] Local_CS318  label="LCS_SideArm_Outer_Screw"
  AttacherType = Attacher::AttachEngine3D
  MapMode = 11
  Placement = pos=(-9e-16,10,0) rot=(0.57735,-0.57735,-0.57735;4.18879rad)
  Support = -> [Pocket189]
FEATURE [PartDesign::CoordinateSystem] Local_CS319  label="LCS_SideArm_Outer_Pivot"
  AttacherType = Attacher::AttachEngine3D
  MapMode = 45
  Placement = pos=(1.21e-14,-0.72,1.5e-15) rot=(0.707107,0,0.707106;3.14159rad)
  Support = -> [Pocket189]
FEATURE [PartDesign::Chamfer] Chamfer  label="SideArm_Outer_Chamfer"
  Angle = 45
  Base = -> Pocket189 [Edge41,Edge40,Edge38,Edge39]
  BaseFeature = -> Pocket189
  ChamferType = 0
  FlipDirection = false
  Placement = pos=(7.75,2.5,15) rot=(0,0,1;0rad)
  Size = 0.4
  Size2 = 1
  SupportTransform = false
  UseAllEdges = false
FEATURE [PartDesign::Body] Body022059  label="SideArm_Pivot_Outer_Square"
  Group = -> [Sketch263,Sketch264,Sketch265,Local_CS315,Local_CS316,Pad066,Pocket176,Pocket177,Cylinder014,Cylinder015,PolarPattern005,Local_CS317,Sketch268,Sketch269,Sketch270,Sketch271,Sketch272,Pocket189,Local_CS,Local_CS318,Local_CS319,Chamfer]
  Origin = -> Origin113
  Tip = -> Chamfer
PROVENANCE & LICENSES
A FreeCAD (.FCStd) document from a public repository crawl; recipes are the document's own serialized feature recipes (and, for linked parts, companion documents' recipes).
License: as declared in the source repository (recorded in the dataset sidecar).
